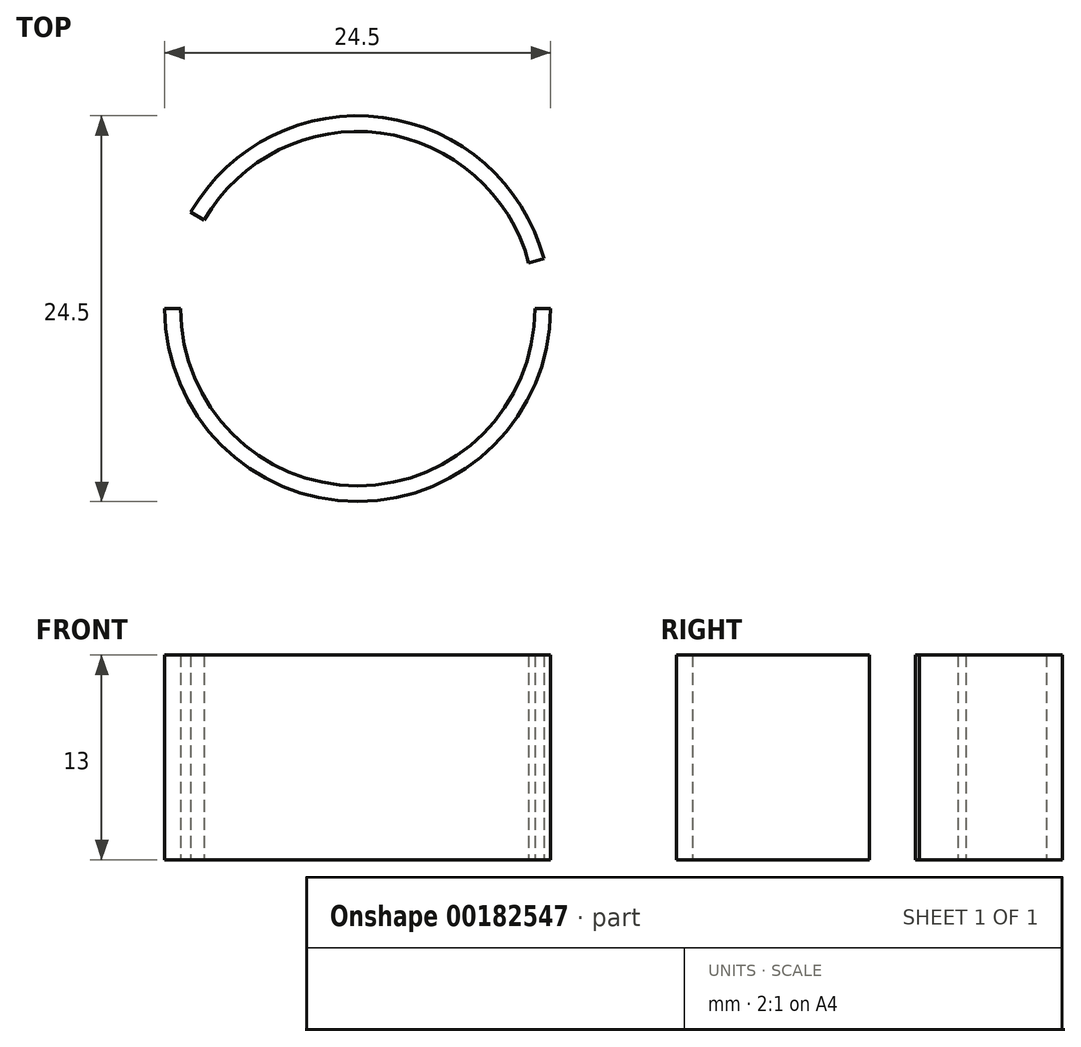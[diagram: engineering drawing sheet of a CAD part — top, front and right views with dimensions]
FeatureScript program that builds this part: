
annotation { "Feature Type Name" : "Feature", "Feature Type Description" : "" }
export const myFeature = defineFeature(function(context is Context, id is Id, definition is map)
    precondition{}
    {
        {
            var Q0;
            Q0=qCreatedBy(makeId("Top.planeOp"),FACE);
            var sketch = newSketch(context, id + "F0", { "sketchPlane" : qUnion([Q0])});
            skArc(sketch, "E0", {"start": v(10.87, 2.91) * mm, "mid": v(1.47, 11.15) * mm, "end": v(-9.74, 5.62) * mm});
            skArc(sketch, "E1", {"start": v(11.83, 3.17) * mm, "mid": v(1.6, 12.15) * mm, "end": v(-10.6, 6.12) * mm});
            skLineSegment(sketch, "E2", {"start": v(-11.25, 0) * mm, "end": v(-12.25, 0) * mm});
            skLineSegment(sketch, "E3", {"start": v(-9.74, 5.62) * mm, "end": v(-10.6, 6.12) * mm});
            skLineSegment(sketch, "E4", {"start": v(11.25, 0) * mm, "end": v(12.25, 0) * mm});
            skLineSegment(sketch, "E5", {"start": v(10.87, 2.91) * mm, "end": v(11.83, 3.17) * mm});
            skArc(sketch, "E6.trimOffspring", {"start": v(-11.25, 0) * mm, "mid": v(0, -11.25) * mm, "end": v(11.25, 0) * mm});
            skArc(sketch, "E7.trimOffspring", {"start": v(-12.25, 0) * mm, "mid": v(0, -12.25) * mm, "end": v(12.25, 0) * mm});
            skSolve(sketch);
        }
        {
            var Q0;
            Q0 = qSketchRegion(id + "F0", true);
            extrude(context, id + "F1", {"entities" : qUnion([Q0]), "depth" : 13 * mm});
        }
    });
